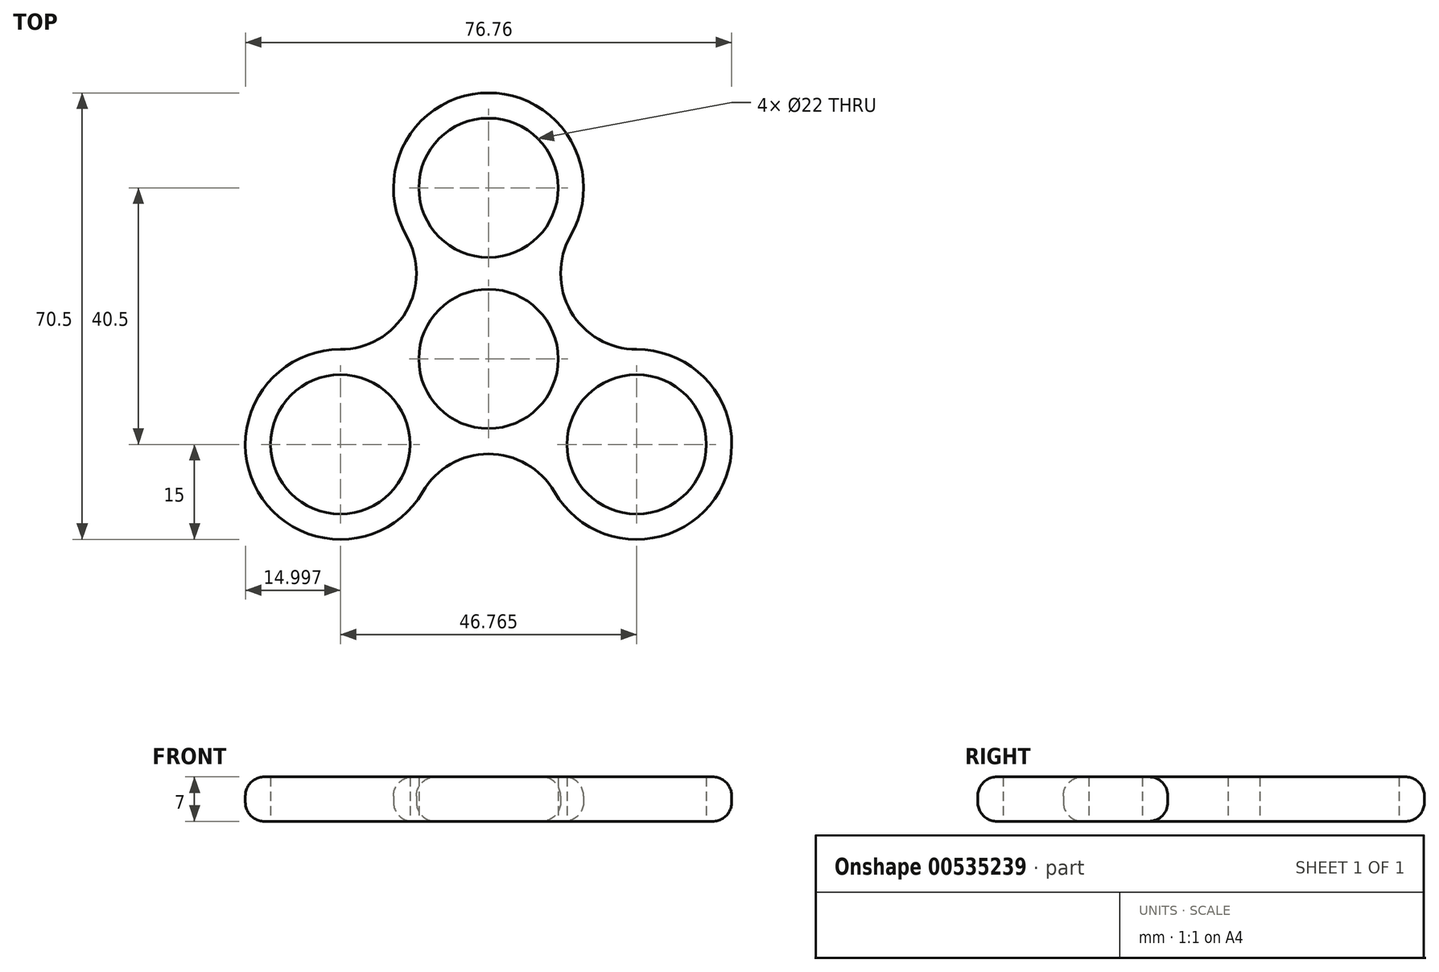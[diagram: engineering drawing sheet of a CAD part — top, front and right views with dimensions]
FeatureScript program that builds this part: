
annotation { "Feature Type Name" : "Feature", "Feature Type Description" : "" }
export const myFeature = defineFeature(function(context is Context, id is Id, definition is map)
    precondition{}
    {
        {
            var Q0;
            Q0=qCreatedBy(makeId("Top.planeOp"),FACE);
            var sketch = newSketch(context, id + "F0", { "sketchPlane" : qUnion([Q0])});
            skCircle(sketch, "E0", {"center": v(0, 0) * mm, "radius": 11 * mm});
            skLineSegment(sketch, "E1", {"start": v(0, 0) * mm, "end": v(0, 27) * mm});
            skCircle(sketch, "E2", {"center": v(0, 27) * mm, "radius": 11 * mm});
            skCircle(sketch, "E3.0", {"center": v(0, 27) * mm, "radius": 15 * mm});
            skCircle(sketch, "E4.1.0", {"center": v(-23.38, -13.5) * mm, "radius": 15 * mm});
            skCircle(sketch, "E4.1.1", {"center": v(-23.38, -13.5) * mm, "radius": 11 * mm});
            skCircle(sketch, "E4.2.0", {"center": v(23.38, -13.5) * mm, "radius": 15 * mm});
            skCircle(sketch, "E4.2.1", {"center": v(23.38, -13.5) * mm, "radius": 11 * mm});
            skPoint(sketch, "E5", {"position": v(0, 11) * mm});
            skArc(sketch, "E6", {"start": v(-23.38, 1.5) * mm, "mid": v(-13, 7.5) * mm, "end": v(-13, 19.5) * mm});
            skArc(sketch, "E7.1.0", {"start": v(10.4, -21) * mm, "mid": v(0, -15) * mm, "end": v(-10.4, -21) * mm});
            skArc(sketch, "E7.2.0", {"start": v(13, 19.5) * mm, "mid": v(13, 7.5) * mm, "end": v(23.38, 1.5) * mm});
            skSolve(sketch);
        }
        {
            var Q0;
            Q0=makeQuery(id+"F0.imprint","IMPRINT",FACE,{"disambiguationData":[TD([[makeQuery(id+"F0.imprint","IMPRINT",EDGE,{"derivedFrom":sQuery(id+"F0.wireOp",EDGE,"E0")}),-1.0]])]});
            var Q1;
            Q1=makeQuery(id+"F0.imprint","IMPRINT",FACE,{"disambiguationData":[TD([[makeQuery(id+"F0.imprint","IMPRINT",EDGE,{"derivedFrom":sQuery(id+"F0.wireOp",EDGE,"E2")}),-1.0]])]});
            var Q2;
            Q2=makeQuery(id+"F0.imprint","IMPRINT",FACE,{"disambiguationData":[TD([[makeQuery(id+"F0.imprint","IMPRINT",EDGE,{"derivedFrom":sQuery(id+"F0.wireOp",EDGE,"E4.1.1")}),-1.0]])]});
            var Q3;
            Q3=makeQuery(id+"F0.imprint","IMPRINT",FACE,{"disambiguationData":[TD([[makeQuery(id+"F0.imprint","IMPRINT",EDGE,{"derivedFrom":sQuery(id+"F0.wireOp",EDGE,"E4.2.1")}),-1.0]])]});
            extrude(context, id + "F1", {"entities" : qUnion([Q0, Q1, Q2, Q3]), "endBound" : BoundingType.SYMMETRIC, "depth" : 7 * mm, "offsetDistance" : 25 * mm});
        }
        {
            var Q0;
            Q0=makeQuery(id+"F1.opExtrude","CAP_EDGE",EDGE,{"disambiguationData":[OSD([sQuery(id+"F0.wireOp",EDGE,"E3.0")])],"isStart":false});
            var Q1;
            Q1=makeQuery(id+"F1.opExtrude","CAP_EDGE",EDGE,{"disambiguationData":[OSD([sQuery(id+"F0.wireOp",EDGE,"E4.1.0")])],"isStart":true});
            fillet(context, id + "F2", {"entities" : qUnion([Q0, Q1]), "radius" : 3 * mm, "tangentPropagation" : true, "allowEdgeOverflow" : false});
        }
    });
